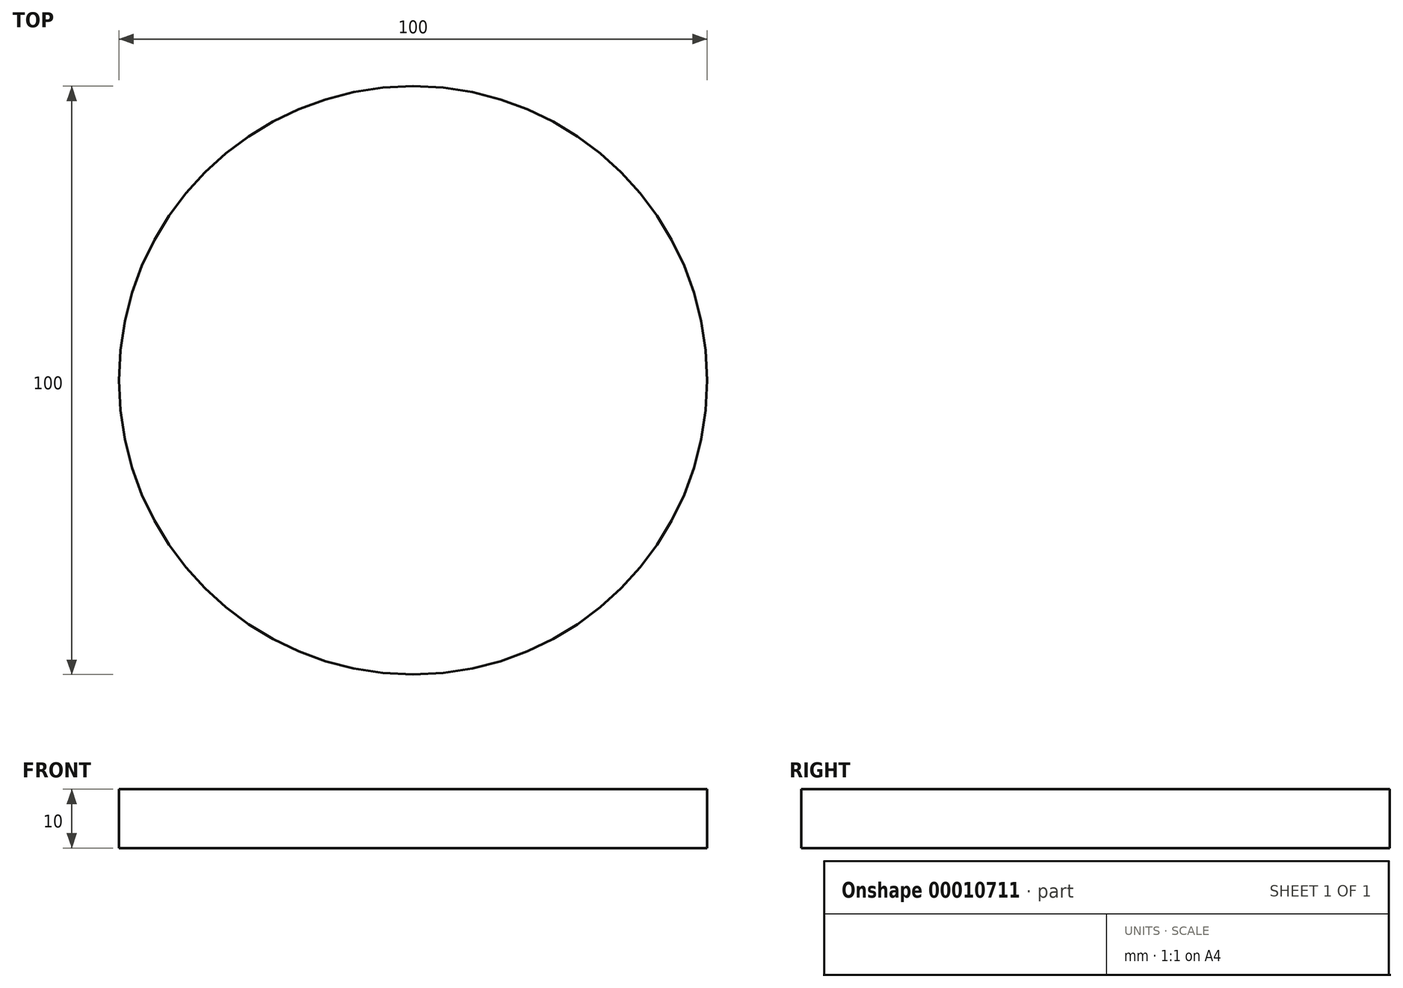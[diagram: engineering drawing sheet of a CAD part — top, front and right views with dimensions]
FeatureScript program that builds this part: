
annotation { "Feature Type Name" : "Feature", "Feature Type Description" : "" }
export const myFeature = defineFeature(function(context is Context, id is Id, definition is map)
    precondition{}
    {
        {
            var Q0;
            Q0=qCreatedBy(makeId("Top.planeOp"),FACE);
            var sketch = newSketch(context, id + "F0", { "sketchPlane" : qUnion([Q0])});
            skCircle(sketch, "E0", {"center": v(0, 0) * mm, "radius": 50 * mm});
            skCircle(sketch, "E1", {"center": v(0, 0) * mm, "radius": 50.55 * mm});
            skSolve(sketch);
        }
        {
            var Q0;
            Q0=makeQuery(id+"F0.imprint","IMPRINT",FACE,{"disambiguationData":[TD([[makeQuery(id+"F0.imprint","IMPRINT",EDGE,{"derivedFrom":sQuery(id+"F0.wireOp",EDGE,"E0")}),1.0]])]});
            extrude(context, id + "F1", {"entities" : qUnion([Q0]), "depth" : 10 * mm});
        }
    });
